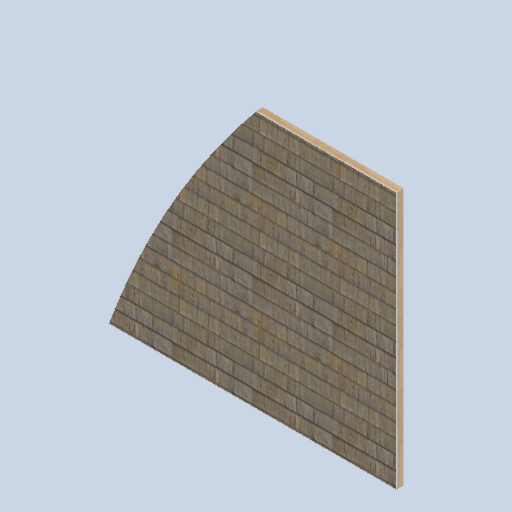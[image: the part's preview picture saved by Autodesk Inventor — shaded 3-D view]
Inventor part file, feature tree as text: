
AUTODESK INVENTOR PART (.ipt)
format: ipt  version: 2024.2 (Build 282272000, 272)  size: 403,456 bytes
history: native  units: mm
features: extrude x1, sketch x1
ambient origin geometry x8: Origin, YZ Plane, XZ Plane, XY Plane, X Axis, Y Axis, Z Axis, Center Point
bodies: Solid1 (feature_tree)
feature tree (2):
  extrude  "Extrusion1"  [1 undecoded]
  sketch  "Sketch1"  dims[d0=80.0mm d1=0.0mm]
note: 1 required parameter value undecoded (feature->parameter linkage not recoverable at this tier; creation-order binding heuristic only, values carry confidence <= 0.55)
